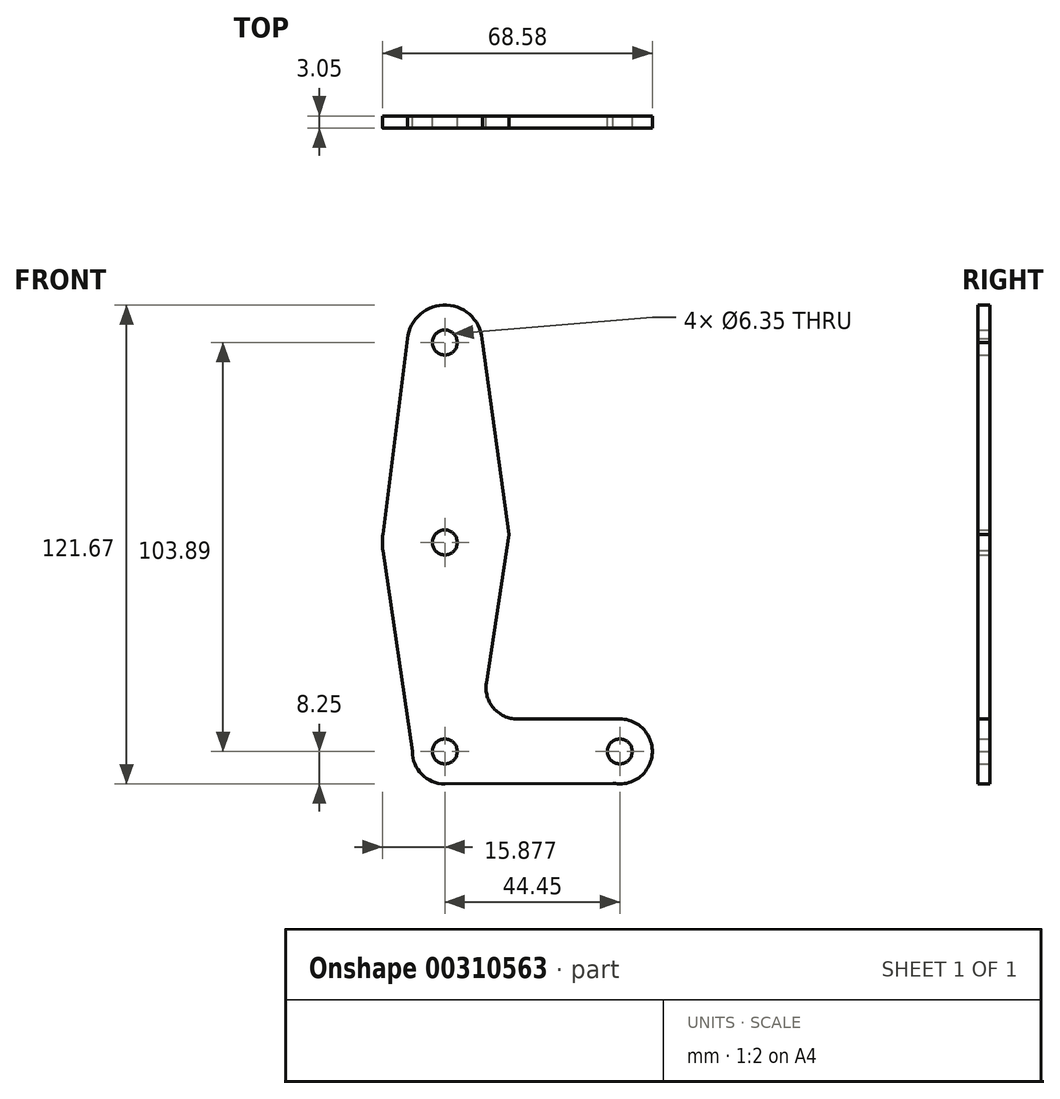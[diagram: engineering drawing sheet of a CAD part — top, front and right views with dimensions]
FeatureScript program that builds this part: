
annotation { "Feature Type Name" : "Feature", "Feature Type Description" : "" }
export const myFeature = defineFeature(function(context is Context, id is Id, definition is map)
    precondition{}
    {
        {
            var Q0;
            Q0=qCreatedBy(makeId("Front.planeOp"),FACE);
            var sketch = newSketch(context, id + "F0", { "sketchPlane" : qUnion([Q0])});
            skLineSegment(sketch, "E0", {"start": v(-39.55, 39.46) * mm, "end": v(-39.55, -74.84) * mm, "construction": true});
            skLineSegment(sketch, "E1", {"start": v(-19.13, -74.84) * mm, "end": v(-19.13, -11.34) * mm, "construction": true});
            skLineSegment(sketch, "E2", {"start": v(-19.13, -64.43) * mm, "end": v(25.32, -64.43) * mm, "construction": true});
            skCircle(sketch, "E3", {"center": v(-9.82, 39.46) * mm, "radius": 9.53 * mm});
            skCircle(sketch, "E4", {"center": v(-9.82, -11.34) * mm, "radius": 15.88 * mm});
            skCircle(sketch, "E5", {"center": v(-9.82, -64.43) * mm, "radius": 8.26 * mm});
            skLineSegment(sketch, "E6", {"start": v(-9.82, -64.43) * mm, "end": v(34.63, -64.43) * mm, "construction": true});
            skCircle(sketch, "E7", {"center": v(34.63, -64.43) * mm, "radius": 8.26 * mm});
            skLineSegment(sketch, "E8", {"start": v(-19.3, 40.45) * mm, "end": v(-25.57, -9.35) * mm});
            skLineSegment(sketch, "E9", {"start": v(-25.57, -13.32) * mm, "end": v(-18.08, -64.43) * mm});
            skLineSegment(sketch, "E10", {"start": v(0.73, -47.01) * mm, "end": v(6.55, -9.35) * mm});
            skLineSegment(sketch, "E11", {"start": v(-0.3, 39.46) * mm, "end": v(6.55, -9.35) * mm});
            skLineSegment(sketch, "E12", {"start": v(-9.82, -72.68) * mm, "end": v(36.4, -72.5) * mm});
            skLineSegment(sketch, "E13", {"start": v(8.59, -56.17) * mm, "end": v(36.4, -56.17) * mm});
            skPoint(sketch, "E14.newPointB", {"position": v(-9.82, -56.17) * mm});
            skArc(sketch, "E14.filletArc", {"start": v(0.73, -47.01) * mm, "mid": v(2.55, -53.4) * mm, "end": v(8.59, -56.17) * mm});
            skCircle(sketch, "E15", {"center": v(-9.82, -11.34) * mm, "radius": 3.18 * mm});
            skCircle(sketch, "E16", {"center": v(-9.82, -64.43) * mm, "radius": 3.18 * mm});
            skCircle(sketch, "E17", {"center": v(34.63, -64.43) * mm, "radius": 3.18 * mm});
            skCircle(sketch, "E18", {"center": v(-9.82, 39.46) * mm, "radius": 3.18 * mm});
            skSolve(sketch);
        }
        {
            var Q0;
            {var subQ0=sQuery(id+"F0.wireOp",EDGE,"E8");Q0=makeQuery(id+"F0.imprint","IMPRINT",FACE,{"disambiguationData":[TD([[makeQuery(id+"F0.imprint","IMPRINT",EDGE,{"derivedFrom":subQ0}),1.0]])]});}
            var Q1;
            Q1=makeQuery(id+"F0.imprint","IMPRINT",FACE,{"disambiguationData":[TD([[makeQuery(id+"F0.imprint","IMPRINT",EDGE,{"derivedFrom":sQuery(id+"F0.wireOp",EDGE,"E16")}),-1.0]])]});
            var Q2;
            Q2=makeQuery(id+"F0.imprint","IMPRINT",FACE,{"disambiguationData":[TD([[makeQuery(id+"F0.imprint","IMPRINT",EDGE,{"derivedFrom":sQuery(id+"F0.wireOp",EDGE,"E15")}),-1.0]])]});
            var Q3;
            Q3=makeQuery(id+"F0.imprint","IMPRINT",FACE,{"disambiguationData":[TD([[makeQuery(id+"F0.imprint","IMPRINT",EDGE,{"derivedFrom":sQuery(id+"F0.wireOp",EDGE,"E17")}),-1.0]])]});
            var Q4;
            {var subQ13=sQuery(id+"F0.wireOp",EDGE,"E14.filletArc");Q4=makeQuery(id+"F0.imprint","IMPRINT",FACE,{"disambiguationData":[TD([[makeQuery(id+"F0.imprint","IMPRINT",EDGE,{"derivedFrom":subQ13}),-1.0]])]});}
            var Q5;
            {var subQ0=sQuery(id+"F0.wireOp",EDGE,"E12");var subQ1=sQuery(id+"F0.wireOp",EDGE,"E7");var subQ2=makeQuery(id+"F0.imprint","INTERSECT",VERTEX,{"disambiguationData":[OD(0.0)],"derivedFrom":[subQ1,subQ0]});Q5=makeQuery(id+"F0.imprint","IMPRINT",FACE,{"disambiguationData":[TD([[makeQuery(id+"F0.imprint","IMPRINT",EDGE,{"disambiguationData":[TD([[subQ2,1.0]])],"derivedFrom":subQ1}),1.0]])]});}
            var Q6;
            {var subQ0=sQuery(id+"F0.wireOp",EDGE,"E9");var subQ1=sQuery(id+"F0.wireOp",EDGE,"E4");var subQ2=makeQuery(id+"F0.imprint","INTERSECT",VERTEX,{"disambiguationData":[OD(0.0)],"derivedFrom":[subQ1,subQ0]});Q6=makeQuery(id+"F0.imprint","IMPRINT",FACE,{"disambiguationData":[TD([[makeQuery(id+"F0.imprint","IMPRINT",EDGE,{"disambiguationData":[TD([[subQ2,-1.0]])],"derivedFrom":subQ1}),1.0]])]});}
            var Q7;
            Q7=makeQuery(id+"F0.imprint","IMPRINT",FACE,{"disambiguationData":[TD([[makeQuery(id+"F0.imprint","IMPRINT",EDGE,{"derivedFrom":sQuery(id+"F0.wireOp",EDGE,"E18")}),-1.0]])]});
            extrude(context, id + "F1", {"entities" : qUnion([Q0, Q1, Q2, Q3, Q4, Q5, Q6, Q7]), "depth" : 3.05 * mm});
        }
    });
